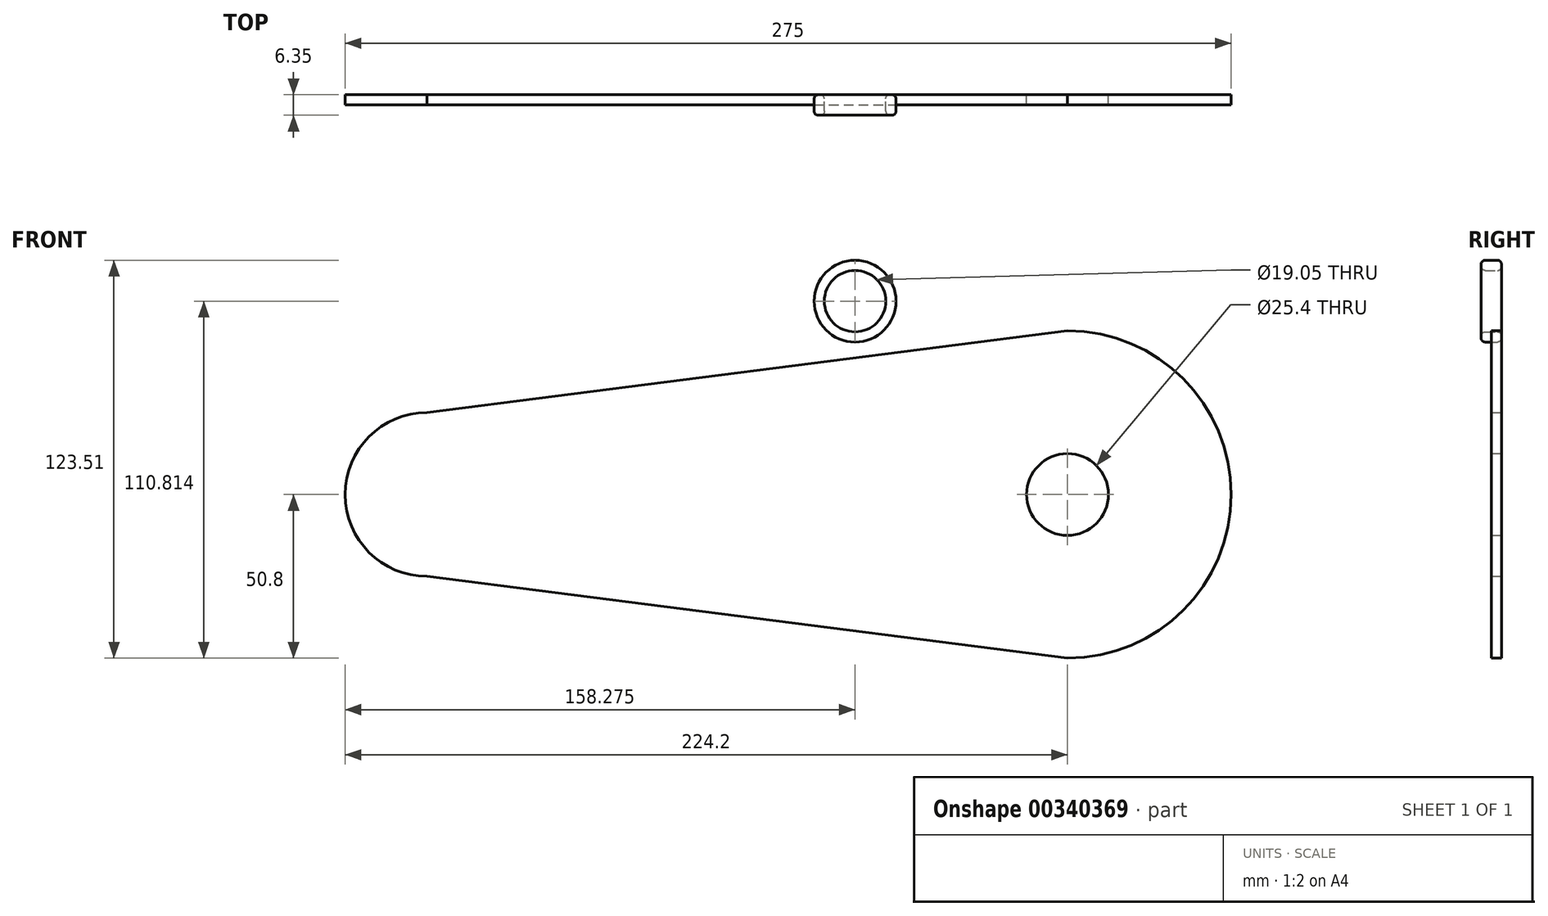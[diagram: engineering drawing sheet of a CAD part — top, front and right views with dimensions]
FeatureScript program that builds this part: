
annotation { "Feature Type Name" : "Feature", "Feature Type Description" : "" }
export const myFeature = defineFeature(function(context is Context, id is Id, definition is map)
    precondition{}
    {
        {
            var Q0;
            Q0=qCreatedBy(makeId("Front.planeOp"),FACE);
            var sketch = newSketch(context, id + "F0", { "sketchPlane" : qUnion([Q0])});
            skCircle(sketch, "E0", {"center": v(0, 0) * mm, "radius": 50.8 * mm});
            skCircle(sketch, "E1", {"center": v(-198.8, 0) * mm, "radius": 25.4 * mm});
            skLineSegment(sketch, "E2", {"start": v(-198.8, 25.4) * mm, "end": v(0, 50.8) * mm});
            skLineSegment(sketch, "E3", {"start": v(-198.8, -25.4) * mm, "end": v(0, -50.8) * mm});
            skCircle(sketch, "E4", {"center": v(0, 0) * mm, "radius": 12.7 * mm});
            skSolve(sketch);
        }
        {
            var Q0;
            {var subQ0=sQuery(id+"F0.wireOp",EDGE,"E2");var subQ1=sQuery(id+"F0.wireOp",EDGE,"E0");var subQ2=makeQuery(id+"F0.imprint","INTERSECT",VERTEX,{"disambiguationData":[OD(1.0)],"derivedFrom":[subQ1,subQ0]});Q0=makeQuery(id+"F0.imprint","IMPRINT",FACE,{"disambiguationData":[TD([[makeQuery(id+"F0.imprint","IMPRINT",EDGE,{"disambiguationData":[TD([[subQ2,-1.0]])],"derivedFrom":subQ1}),1.0]])]});}
            var Q1;
            {var subQ0=sQuery(id+"F0.wireOp",EDGE,"E2");var subQ1=sQuery(id+"F0.wireOp",EDGE,"E0");var subQ2=makeQuery(id+"F0.imprint","INTERSECT",VERTEX,{"disambiguationData":[OD(1.0)],"derivedFrom":[subQ1,subQ0]});Q1=makeQuery(id+"F0.imprint","IMPRINT",FACE,{"disambiguationData":[TD([[makeQuery(id+"F0.imprint","IMPRINT",EDGE,{"disambiguationData":[TD([[subQ2,-1.0]])],"derivedFrom":subQ1}),-1.0]])]});}
            var Q2;
            {var subQ0=sQuery(id+"F0.wireOp",EDGE,"E1");var subQ1=makeQuery(id+"F0.imprint","INTERSECT",VERTEX,{"derivedFrom":[subQ0,sQuery(id+"F0.wireOp",EDGE,"E2")]});Q2=makeQuery(id+"F0.imprint","IMPRINT",FACE,{"disambiguationData":[TD([[makeQuery(id+"F0.imprint","IMPRINT",EDGE,{"disambiguationData":[TD([[subQ1,-1.0]])],"derivedFrom":subQ0}),1.0]])]});}
            extrude(context, id + "F1", {"entities" : qUnion([Q0, Q1, Q2]), "depth" : 3.17 * mm});
        }
        {
            var Q0;
            Q0=qCreatedBy(makeId("Front.planeOp"),FACE);
            var sketch = newSketch(context, id + "F2", { "sketchPlane" : qUnion([Q0])});
            skCircle(sketch, "E5", {"center": v(-65.92, 60.01) * mm, "radius": 12.7 * mm});
            skCircle(sketch, "E6", {"center": v(-65.92, 60.01) * mm, "radius": 9.53 * mm});
            skSolve(sketch);
        }
        {
            var Q0;
            Q0=makeQuery(id+"F2.imprint","IMPRINT",FACE,{"disambiguationData":[TD([[makeQuery(id+"F2.imprint","IMPRINT",EDGE,{"derivedFrom":sQuery(id+"F2.wireOp",EDGE,"E5")}),1.0]])]});
            extrude(context, id + "F3", {"entities" : qUnion([Q0]), "depth" : 6.35 * mm});
        }
        {
            var Q0;
            Q0=makeQuery(id+"F3.opExtrude","CAP_EDGE",EDGE,{"disambiguationData":[OSD([sQuery(id+"F2.wireOp",EDGE,"E5")])],"isStart":false});
            var Q1;
            Q1=makeQuery(id+"F3.opExtrude","CAP_EDGE",EDGE,{"disambiguationData":[OSD([sQuery(id+"F2.wireOp",EDGE,"E5")])],"isStart":true});
            var Q2;
            Q2=makeQuery(id+"F3.opExtrude","CAP_EDGE",EDGE,{"disambiguationData":[OSD([sQuery(id+"F2.wireOp",EDGE,"E6")])],"isStart":false});
            var Q3;
            Q3=makeQuery(id+"F3.opExtrude","CAP_EDGE",EDGE,{"disambiguationData":[OSD([sQuery(id+"F2.wireOp",EDGE,"E6")])],"isStart":true});
            fillet(context, id + "F4", {"entities" : qUnion([Q0, Q1, Q2, Q3]), "radius" : 1.27 * mm, "tangentPropagation" : true, "allowEdgeOverflow" : false});
        }
    });
